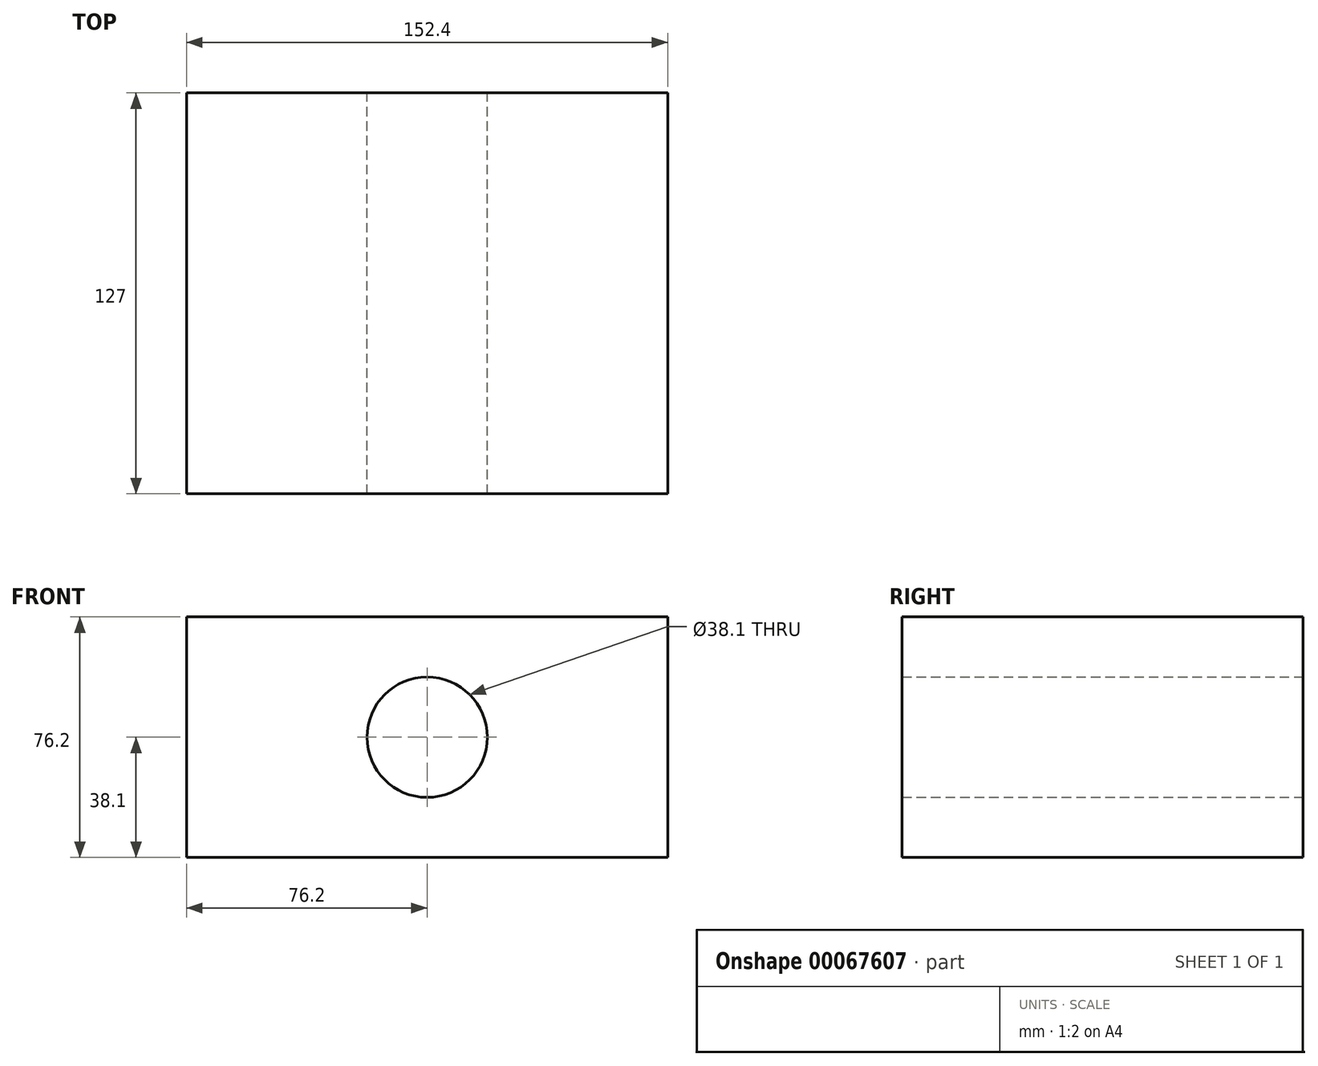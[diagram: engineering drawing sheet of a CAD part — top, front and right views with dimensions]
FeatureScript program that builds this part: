
annotation { "Feature Type Name" : "Feature", "Feature Type Description" : "" }
export const myFeature = defineFeature(function(context is Context, id is Id, definition is map)
    precondition{}
    {
        {
            var Q0;
            Q0=qCreatedBy(makeId("Front.planeOp"),FACE);
            var sketch = newSketch(context, id + "F0", { "sketchPlane" : qUnion([Q0])});
            skLineSegment(sketch, "E0.rect.bottom", {"start": v(-76.2, 38.1) * mm, "end": v(76.2, 38.1) * mm});
            skLineSegment(sketch, "E0.rect.top", {"start": v(-76.2, -38.1) * mm, "end": v(76.2, -38.1) * mm});
            skLineSegment(sketch, "E0.rect.left", {"start": v(-76.2, 38.1) * mm, "end": v(-76.2, -38.1) * mm});
            skLineSegment(sketch, "E0.rect.right", {"start": v(76.2, 38.1) * mm, "end": v(76.2, -38.1) * mm});
            skPoint(sketch, "E0.rect.middle", {"position": v(0, 0) * mm});
            skCircle(sketch, "E1", {"center": v(0, 0) * mm, "radius": 19.05 * mm});
            skSolve(sketch);
        }
        {
            var Q0;
            Q0=makeQuery(id+"F0.imprint","IMPRINT",FACE,{"disambiguationData":[TD([[makeQuery(id+"F0.imprint","IMPRINT",EDGE,{"derivedFrom":sQuery(id+"F0.wireOp",EDGE,"E0.rect.bottom")}),-1.0]])]});
            extrude(context, id + "F1", {"entities" : qUnion([Q0]), "flatOperationType" : FlatOperationType.REMOVE, "offsetDistance" : 25.4 * mm, "depth" : 127 * mm, "domain" : OperationDomain.MODEL, "symmetric" : true});
        }
    });
